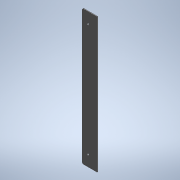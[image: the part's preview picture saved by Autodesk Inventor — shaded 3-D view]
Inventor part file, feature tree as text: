
AUTODESK INVENTOR PART (.ipt)
format: ipt  version: 2021.3 (Build 253353000, 353)  size: 120,320 bytes
history: native  units: mm
features: sketch x3, extrude x2, hole x1, fillet x1
ambient origin geometry x8: Origin, YZ Plane, XZ Plane, XY Plane, X Axis, Y Axis, Z Axis, Center Point
bodies: Volumenkörper1 (feature_tree)
feature tree (7):
  extrude  "Extrusion1"  Depth=1.5mm
  hole  "Bohrung1"  [1 undecoded]
  extrude  "Extrusion2"  Depth=3.0mm
  fillet  "Rundung1"  Radius=20.0mm
  sketch  "Skizze1"  dims[d0=40.0mm d1=1.5mm]
  sketch  "Skizze2"  dims[d2=298.0mm d3=0.0mm d4=250.0mm]
  sketch  "Skizze3"  dims[d5=298.0mm d6=24.0mm d7=20.0mm d8=20.0mm d9=4.5mm d10=6.0mm d11=4.0mm d12=2.0mm d13=90.0deg d14=11.8mm d15=20.594885mm d16=7.0mm d17=298.0mm d18=298.0mm d19=0.0mm d20=3.0mm]
note: 1 required parameter value undecoded (feature->parameter linkage not recoverable at this tier; creation-order binding heuristic only, values carry confidence <= 0.55)
